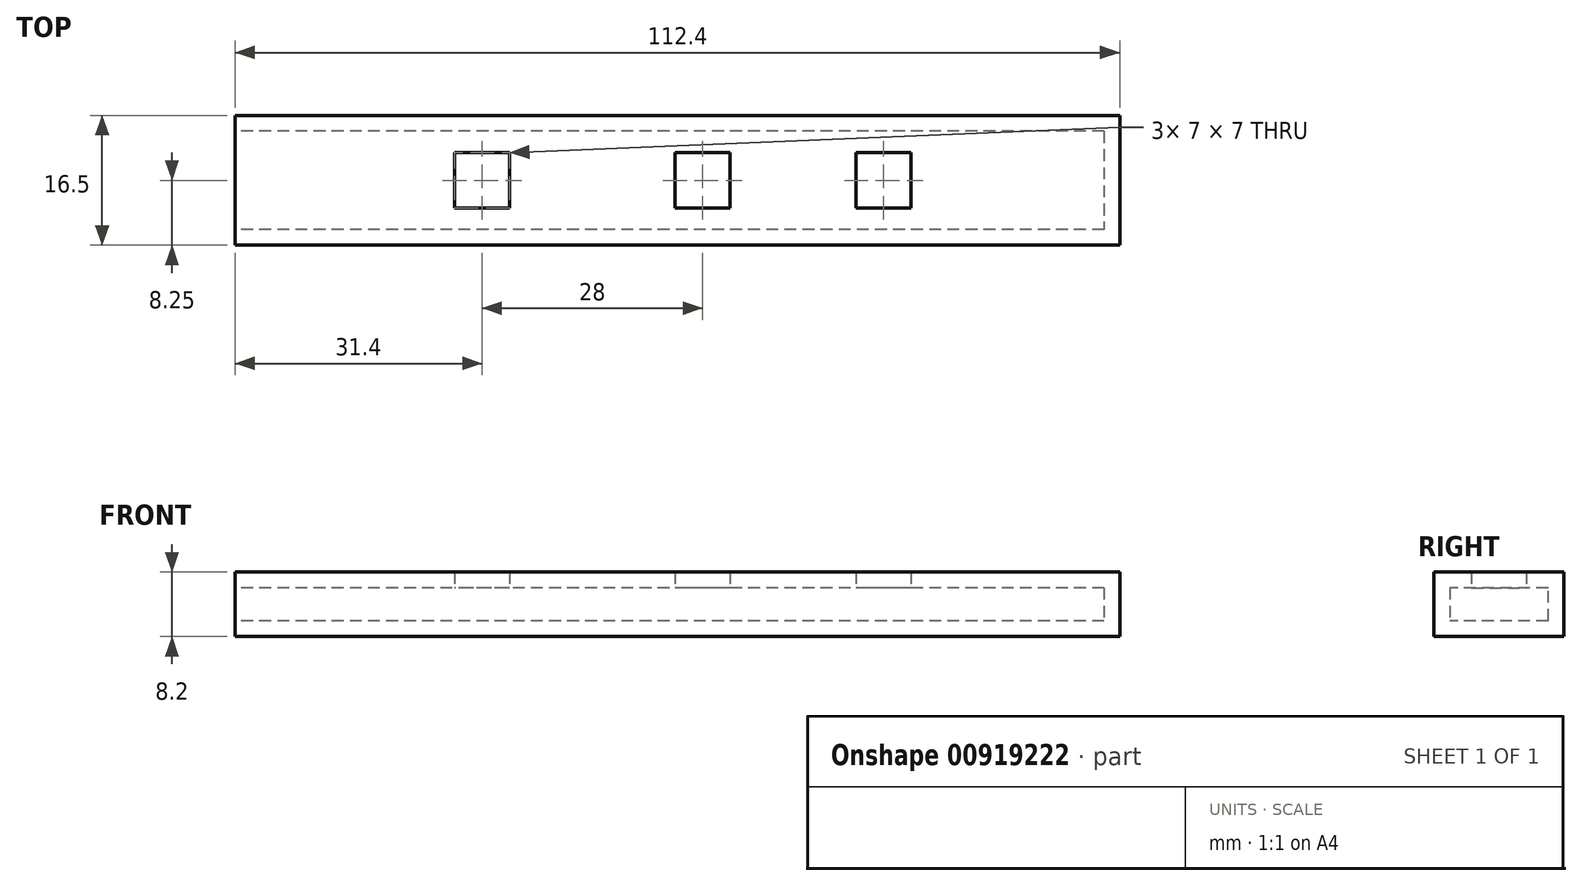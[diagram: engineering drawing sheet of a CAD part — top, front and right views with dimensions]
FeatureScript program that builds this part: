
annotation { "Feature Type Name" : "Feature", "Feature Type Description" : "" }
export const myFeature = defineFeature(function(context is Context, id is Id, definition is map)
    precondition{}
    {
        {
            assignVariable(context, id + "F0", {"name" : "thickness", "anyValue" : 2});
        }
        {
            assignVariable(context, id + "F1", {"name" : "padding", "anyValue" : 0.2});
        }
        {
            var Q0;
            Q0=qCreatedBy(makeId("Top.planeOp"),FACE);
            var sketch = newSketch(context, id + "F2", { "sketchPlane" : qUnion([Q0])});
            skLineSegment(sketch, "E0", {"start": v(30.7, -3.5) * mm, "end": v(30.7, 3.5) * mm});
            skLineSegment(sketch, "E1", {"start": v(30.7, 3.5) * mm, "end": v(23.7, 3.5) * mm});
            skLineSegment(sketch, "E2.bottom", {"start": v(7.7, -3.5) * mm, "end": v(0.7, -3.5) * mm});
            skLineSegment(sketch, "E2.top", {"start": v(7.7, 3.5) * mm, "end": v(0.7, 3.5) * mm});
            skLineSegment(sketch, "E2.left", {"start": v(7.7, -3.5) * mm, "end": v(7.7, 3.5) * mm});
            skLineSegment(sketch, "E2.right", {"start": v(0.7, -3.5) * mm, "end": v(0.7, 3.5) * mm});
            skLineSegment(sketch, "E3.bottom", {"start": v(-20.3, -3.5) * mm, "end": v(-27.3, -3.5) * mm});
            skLineSegment(sketch, "E3.top", {"start": v(-20.3, 3.5) * mm, "end": v(-27.3, 3.5) * mm});
            skLineSegment(sketch, "E3.left", {"start": v(-20.3, -3.5) * mm, "end": v(-20.3, 3.5) * mm});
            skLineSegment(sketch, "E3.right", {"start": v(-27.3, -3.5) * mm, "end": v(-27.3, 3.5) * mm});
            skPoint(sketch, "E4", {"position": v(30.7, 0) * mm});
            skPoint(sketch, "E5", {"position": v(7.7, 0) * mm});
            skLineSegment(sketch, "E6", {"start": v(30.7, -3.5) * mm, "end": v(23.7, -3.5) * mm});
            skLineSegment(sketch, "E7", {"start": v(23.7, -3.5) * mm, "end": v(23.7, 3.5) * mm});
            skPoint(sketch, "E8", {"position": v(-20.3, 0) * mm});
            skLineSegment(sketch, "E9.bottom", {"start": v(55.2, -6.25) * mm, "end": v(-55.2, -6.25) * mm});
            skLineSegment(sketch, "E9.top", {"start": v(55.2, 6.25) * mm, "end": v(-55.2, 6.25) * mm});
            skLineSegment(sketch, "E9.right", {"start": v(-55.2, -6.25) * mm, "end": v(-55.2, 6.25) * mm});
            skLineSegment(sketch, "E10", {"start": v(55.2, 6.25) * mm, "end": v(55.2, -6.25) * mm});
            skPoint(sketch, "E11", {"position": v(55.2, 0) * mm});
            skPoint(sketch, "E12", {"position": v(0, 6.25) * mm});
            skSolve(sketch);
        }
        {
            var Q0;
            Q0=makeQuery(id+"F2.imprint","IMPRINT",FACE,{"disambiguationData":[TD([[makeQuery(id+"F2.imprint","IMPRINT",EDGE,{"derivedFrom":sQuery(id+"F2.wireOp",EDGE,"E0")}),-1.0]])]});
            extrude(context, id + "F3", {"entities" : qUnion([Q0]), "depth" : (getVariable(context, 'thickness')) * mm, "offsetDistance" : 25 * mm});
        }
        {
            var Q0;
            Q0=makeQuery(id+"F3.opExtrude","SWEPT_FACE",FACE,{"disambiguationData":[OSD([sQuery(id+"F2.wireOp",EDGE,"E9.bottom")])]});
            extrude(context, id + "F4", {"entities" : qUnion([Q0]), "operationType" : NewBodyOperationType.ADD, "depth" : (getVariable(context, 'thickness')) * mm, "offsetDistance" : 25 * mm});
        }
        {
            var Q0;
            Q0=makeQuery(id+"F3.opExtrude","SWEPT_FACE",FACE,{"disambiguationData":[OSD([sQuery(id+"F2.wireOp",EDGE,"E9.top")])]});
            extrude(context, id + "F5", {"entities" : qUnion([Q0]), "operationType" : NewBodyOperationType.ADD, "depth" : (getVariable(context, 'thickness')) * mm, "offsetDistance" : 25 * mm});
        }
        {
            var Q0;
            {var subQ0=sQuery(id+"F2.wireOp",EDGE,"E9.right");Q0=makeQuery(id+"F5.boolean.opBoolean","MERGE",FACE,{"derivedFrom":[makeQuery(id+"F4.boolean.opBoolean","MERGE",FACE,{"derivedFrom":[makeQuery(id+"F3.opExtrude","SWEPT_FACE",FACE,{"disambiguationData":[OSD([subQ0])]}),makeQuery(id+"F4.opExtrude","SWEPT_FACE",FACE,{"disambiguationData":[OSD([sQuery(id+"F2.wireOp",EDGE,"E9.bottom"),subQ0])]})]}),makeQuery(id+"F5.opExtrude","SWEPT_FACE",FACE,{"disambiguationData":[OSD([sQuery(id+"F2.wireOp",EDGE,"E9.top"),subQ0])]})]});}
            var sketch = newSketch(context, id + "F6", { "sketchPlane" : qUnion([Q0])});
            skLineSegment(sketch, "E13", {"start": v(-8.25, 0) * mm, "end": v(-8.25, -4.2) * mm});
            skLineSegment(sketch, "E14", {"start": v(-8.25, -4.2) * mm, "end": v(8.25, -4.2) * mm});
            skLineSegment(sketch, "E15", {"start": v(8.25, -4.2) * mm, "end": v(8.25, 0) * mm});
            skLineSegment(sketch, "E16", {"start": v(8.25, 0) * mm, "end": v(-8.25, 0) * mm});
            skLineSegment(sketch, "E17", {"start": v(-6.25, -4.2) * mm, "end": v(-6.25, 0) * mm});
            skLineSegment(sketch, "E18", {"start": v(6.25, 0) * mm, "end": v(6.25, -4.2) * mm});
            skLineSegment(sketch, "E19", {"start": v(-8.25, -4.2) * mm, "end": v(-8.25, -6.2) * mm});
            skLineSegment(sketch, "E20", {"start": v(-8.25, -6.2) * mm, "end": v(8.25, -6.2) * mm});
            skLineSegment(sketch, "E21", {"start": v(8.25, -6.2) * mm, "end": v(8.25, -4.2) * mm});
            skSolve(sketch);
        }
        {
            var Q0;
            {var subQ0=sQuery(id+"F6.wireOp",EDGE,"E15");Q0=makeQuery(id+"F6.imprint","IMPRINT",FACE,{"disambiguationData":[TD([[makeQuery(id+"F6.imprint","IMPRINT",EDGE,{"derivedFrom":subQ0}),1.0]])]});}
            var Q1;
            {var subQ0=sQuery(id+"F6.wireOp",EDGE,"E19");Q1=makeQuery(id+"F6.imprint","IMPRINT",FACE,{"disambiguationData":[TD([[makeQuery(id+"F6.imprint","IMPRINT",EDGE,{"derivedFrom":subQ0}),1.0]])]});}
            var Q2;
            {var subQ0=sQuery(id+"F6.wireOp",EDGE,"E13");Q2=makeQuery(id+"F6.imprint","IMPRINT",FACE,{"disambiguationData":[TD([[makeQuery(id+"F6.imprint","IMPRINT",EDGE,{"derivedFrom":subQ0}),1.0]])]});}
            extrude(context, id + "F7", {"entities" : qUnion([Q0, Q1, Q2]), "operationType" : NewBodyOperationType.ADD, "oppositeDirection" : true, "depth" : (110 + getVariable(context, 'padding') * 2) * mm, "offsetDistance" : 25 * mm});
        }
        {
            var Q0;
            {var subQ0=sQuery(id+"F2.wireOp",EDGE,"E10");Q0=makeQuery(id+"F7.boolean.opBoolean","MERGE",FACE,{"derivedFrom":[makeQuery(id+"F5.boolean.opBoolean","MERGE",FACE,{"derivedFrom":[makeQuery(id+"F4.boolean.opBoolean","MERGE",FACE,{"derivedFrom":[makeQuery(id+"F3.opExtrude","SWEPT_FACE",FACE,{"disambiguationData":[OSD([subQ0])]}),makeQuery(id+"F4.opExtrude","SWEPT_FACE",FACE,{"disambiguationData":[OSD([sQuery(id+"F2.wireOp",EDGE,"E9.bottom"),subQ0])]})]}),makeQuery(id+"F5.opExtrude","SWEPT_FACE",FACE,{"disambiguationData":[OSD([sQuery(id+"F2.wireOp",EDGE,"E9.top"),subQ0])]})]}),makeQuery(id+"F7.opExtrude","CAP_FACE",FACE,{"disambiguationData":[OSD([sQuery(id+"F6.wireOp",EDGE,"E13"),sQuery(id+"F6.wireOp",EDGE,"E14"),sQuery(id+"F6.wireOp",EDGE,"E15"),sQuery(id+"F6.wireOp",EDGE,"E16"),sQuery(id+"F6.wireOp",EDGE,"E17"),sQuery(id+"F6.wireOp",EDGE,"E18"),sQuery(id+"F6.wireOp",EDGE,"E19"),sQuery(id+"F6.wireOp",EDGE,"E20"),sQuery(id+"F6.wireOp",EDGE,"E21")])],"isStart":false})]});}
            var sketch = newSketch(context, id + "F8", { "sketchPlane" : qUnion([Q0])});
            skLineSegment(sketch, "E22.bottom", {"start": v(8.25, -6.2) * mm, "end": v(-8.25, -6.2) * mm});
            skLineSegment(sketch, "E22.top", {"start": v(8.25, 2) * mm, "end": v(-8.25, 2) * mm});
            skLineSegment(sketch, "E22.left", {"start": v(8.25, -6.2) * mm, "end": v(8.25, 2) * mm});
            skLineSegment(sketch, "E22.right", {"start": v(-8.25, -6.2) * mm, "end": v(-8.25, 2) * mm});
            skSolve(sketch);
        }
        {
            var Q0;
            Q0 = qSketchRegion(id + "F8", true);
            extrude(context, id + "F9", {"entities" : qUnion([Q0]), "operationType" : NewBodyOperationType.ADD, "depth" : (getVariable(context, 'thickness')) * mm, "offsetDistance" : 25 * mm});
        }
    });
